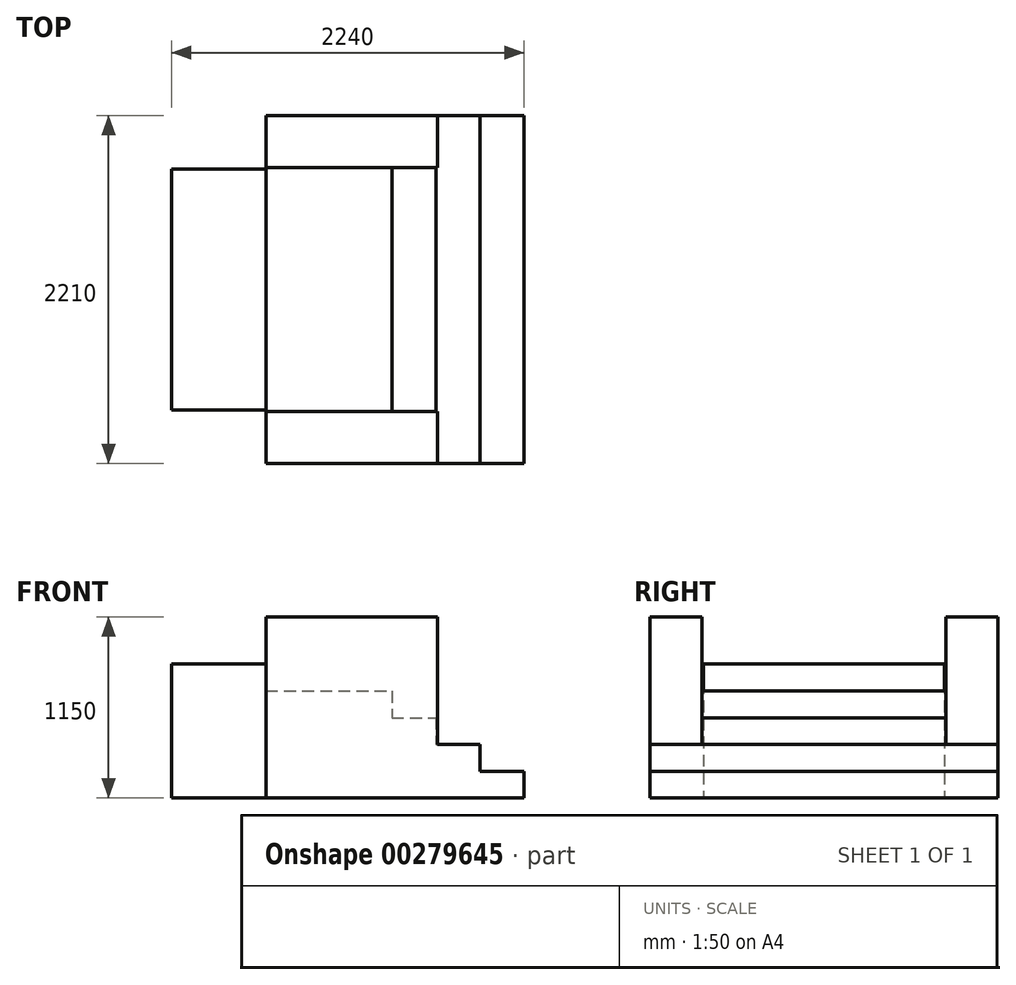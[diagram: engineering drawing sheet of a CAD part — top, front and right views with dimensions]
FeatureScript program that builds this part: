
annotation { "Feature Type Name" : "Feature", "Feature Type Description" : "" }
export const myFeature = defineFeature(function(context is Context, id is Id, definition is map)
    precondition{}
    {
        {
            var Q0;
            Q0=qCreatedBy(makeId("Front.planeOp"),FACE);
            var sketch = newSketch(context, id + "F0", { "sketchPlane" : qUnion([Q0])});
            skLineSegment(sketch, "E0", {"start": v(0, 0) * mm, "end": v(600, 0) * mm});
            skLineSegment(sketch, "E1", {"start": v(600, 0) * mm, "end": v(600, -170) * mm});
            skLineSegment(sketch, "E2", {"start": v(600, -170) * mm, "end": v(1400, -170) * mm});
            skLineSegment(sketch, "E3", {"start": v(1400, -170) * mm, "end": v(1400, -340) * mm});
            skLineSegment(sketch, "E4", {"start": v(1400, -340) * mm, "end": v(1680, -340) * mm});
            skLineSegment(sketch, "E5", {"start": v(1680, -340) * mm, "end": v(1680, -510) * mm});
            skLineSegment(sketch, "E6", {"start": v(1680, -510) * mm, "end": v(1960, -510) * mm});
            skLineSegment(sketch, "E7", {"start": v(1960, -510) * mm, "end": v(1960, -680) * mm});
            skLineSegment(sketch, "E8", {"start": v(1960, -680) * mm, "end": v(2240, -680) * mm});
            skLineSegment(sketch, "E9", {"start": v(2240, -680) * mm, "end": v(2240, -850) * mm});
            skLineSegment(sketch, "E10", {"start": v(0, 0) * mm, "end": v(0, -850) * mm});
            skLineSegment(sketch, "E11", {"start": v(0, -850) * mm, "end": v(2240, -850) * mm});
            skSolve(sketch);
        }
        {
            var Q0;
            Q0=makeQuery(id+"F0.imprint","IMPRINT",FACE,{"disambiguationData":[TD([[makeQuery(id+"F0.imprint","IMPRINT",EDGE,{"derivedFrom":sQuery(id+"F0.wireOp",EDGE,"E0")}),-1.0]])]});
            extrude(context, id + "F1", {"entities" : qUnion([Q0]), "endBound" : BoundingType.SYMMETRIC, "depth" : 2210 * mm});
        }
        {
            var Q0;
            Q0=makeQuery(id+"F1.opExtrude","CAP_FACE",FACE,{"disambiguationData":[OSD([sQuery(id+"F0.wireOp",EDGE,"E0"),sQuery(id+"F0.wireOp",EDGE,"E1"),sQuery(id+"F0.wireOp",EDGE,"E2"),sQuery(id+"F0.wireOp",EDGE,"E3"),sQuery(id+"F0.wireOp",EDGE,"E4"),sQuery(id+"F0.wireOp",EDGE,"E5"),sQuery(id+"F0.wireOp",EDGE,"E6"),sQuery(id+"F0.wireOp",EDGE,"E7"),sQuery(id+"F0.wireOp",EDGE,"E8"),sQuery(id+"F0.wireOp",EDGE,"E9"),sQuery(id+"F0.wireOp",EDGE,"E10"),sQuery(id+"F0.wireOp",EDGE,"E11")])],"isStart":false});
            var sketch = newSketch(context, id + "F2", { "sketchPlane" : qUnion([Q0])});
            skLineSegment(sketch, "E12.bottom", {"start": v(600, 0) * mm, "end": v(0, 0) * mm});
            skLineSegment(sketch, "E12.top", {"start": v(600, -850) * mm, "end": v(0, -850) * mm});
            skLineSegment(sketch, "E12.left", {"start": v(600, 0) * mm, "end": v(600, -850) * mm});
            skLineSegment(sketch, "E12.right", {"start": v(0, 0) * mm, "end": v(0, -850) * mm});
            skSolve(sketch);
        }
        {
            var Q0;
            {var subQ1=sQuery(id+"F2.wireOp",EDGE,"E12.bottom");Q0=makeQuery(id+"F2.imprint","IMPRINT",FACE,{"disambiguationData":[TD([[makeQuery(id+"F2.imprint","IMPRINT",EDGE,{"derivedFrom":subQ1}),-1.0]])]});}
            extrude(context, id + "F3", {"entities" : qUnion([Q0]), "operationType" : NewBodyOperationType.REMOVE, "oppositeDirection" : true, "depth" : 340 * mm});
        }
        {
            var Q0;
            Q0=makeQuery(id+"F1.opExtrude","CAP_FACE",FACE,{"disambiguationData":[OSD([sQuery(id+"F0.wireOp",EDGE,"E0"),sQuery(id+"F0.wireOp",EDGE,"E1"),sQuery(id+"F0.wireOp",EDGE,"E2"),sQuery(id+"F0.wireOp",EDGE,"E3"),sQuery(id+"F0.wireOp",EDGE,"E4"),sQuery(id+"F0.wireOp",EDGE,"E5"),sQuery(id+"F0.wireOp",EDGE,"E6"),sQuery(id+"F0.wireOp",EDGE,"E7"),sQuery(id+"F0.wireOp",EDGE,"E8"),sQuery(id+"F0.wireOp",EDGE,"E9"),sQuery(id+"F0.wireOp",EDGE,"E10"),sQuery(id+"F0.wireOp",EDGE,"E11")])],"isStart":true});
            var sketch = newSketch(context, id + "F4", { "sketchPlane" : qUnion([Q0])});
            skLineSegment(sketch, "E13.bottom", {"start": v(-600, 0) * mm, "end": v(0, 0) * mm});
            skLineSegment(sketch, "E13.top", {"start": v(-600, -850) * mm, "end": v(0, -850) * mm});
            skLineSegment(sketch, "E13.left", {"start": v(-600, 0) * mm, "end": v(-600, -850) * mm});
            skLineSegment(sketch, "E13.right", {"start": v(0, 0) * mm, "end": v(0, -850) * mm});
            skSolve(sketch);
        }
        {
            var Q0;
            {var subQ1=sQuery(id+"F4.wireOp",EDGE,"E13.bottom");Q0=makeQuery(id+"F4.imprint","IMPRINT",FACE,{"disambiguationData":[TD([[makeQuery(id+"F4.imprint","IMPRINT",EDGE,{"derivedFrom":subQ1}),1.0]])]});}
            extrude(context, id + "F5", {"entities" : qUnion([Q0]), "operationType" : NewBodyOperationType.REMOVE, "oppositeDirection" : true, "depth" : 340 * mm});
        }
        {
            var Q0;
            Q0=makeQuery(id+"F1.opExtrude","CAP_FACE",FACE,{"disambiguationData":[OSD([sQuery(id+"F0.wireOp",EDGE,"E0"),sQuery(id+"F0.wireOp",EDGE,"E1"),sQuery(id+"F0.wireOp",EDGE,"E2"),sQuery(id+"F0.wireOp",EDGE,"E3"),sQuery(id+"F0.wireOp",EDGE,"E4"),sQuery(id+"F0.wireOp",EDGE,"E5"),sQuery(id+"F0.wireOp",EDGE,"E6"),sQuery(id+"F0.wireOp",EDGE,"E7"),sQuery(id+"F0.wireOp",EDGE,"E8"),sQuery(id+"F0.wireOp",EDGE,"E9"),sQuery(id+"F0.wireOp",EDGE,"E10"),sQuery(id+"F0.wireOp",EDGE,"E11")])],"isStart":false});
            var sketch = newSketch(context, id + "F6", { "sketchPlane" : qUnion([Q0])});
            skLineSegment(sketch, "E14", {"start": v(600, -170) * mm, "end": v(600, 300) * mm});
            skLineSegment(sketch, "E15", {"start": v(600, 300) * mm, "end": v(1690, 300) * mm});
            skLineSegment(sketch, "E16", {"start": v(1690, 300) * mm, "end": v(1690, -510) * mm});
            skLineSegment(sketch, "E17.0", {"start": v(600, -170) * mm, "end": v(1400, -170) * mm});
            skLineSegment(sketch, "E18.0", {"start": v(1400, -170) * mm, "end": v(1400, -340) * mm});
            skLineSegment(sketch, "E19.0", {"start": v(1400, -340) * mm, "end": v(1680, -340) * mm});
            skLineSegment(sketch, "E20.0", {"start": v(1680, -340) * mm, "end": v(1680, -510) * mm});
            skLineSegment(sketch, "E21.0", {"start": v(1680, -510) * mm, "end": v(1690, -510) * mm});
            skPoint(sketch, "E22.orphan", {"position": v(1960, -510) * mm});
            skSolve(sketch);
        }
        {
            var Q0;
            Q0=makeQuery(id+"F6.imprint","IMPRINT",FACE,{"disambiguationData":[TD([[makeQuery(id+"F6.imprint","IMPRINT",EDGE,{"derivedFrom":sQuery(id+"F6.wireOp",EDGE,"E14")}),-1.0]])]});
            extrude(context, id + "F7", {"entities" : qUnion([Q0]), "operationType" : NewBodyOperationType.ADD, "oppositeDirection" : true, "depth" : 330 * mm});
        }
        {
            var Q0;
            Q0=makeQuery(id+"F1.opExtrude","CAP_FACE",FACE,{"disambiguationData":[OSD([sQuery(id+"F0.wireOp",EDGE,"E0"),sQuery(id+"F0.wireOp",EDGE,"E1"),sQuery(id+"F0.wireOp",EDGE,"E2"),sQuery(id+"F0.wireOp",EDGE,"E3"),sQuery(id+"F0.wireOp",EDGE,"E4"),sQuery(id+"F0.wireOp",EDGE,"E5"),sQuery(id+"F0.wireOp",EDGE,"E6"),sQuery(id+"F0.wireOp",EDGE,"E7"),sQuery(id+"F0.wireOp",EDGE,"E8"),sQuery(id+"F0.wireOp",EDGE,"E9"),sQuery(id+"F0.wireOp",EDGE,"E10"),sQuery(id+"F0.wireOp",EDGE,"E11")])],"isStart":true});
            var sketch = newSketch(context, id + "F8", { "sketchPlane" : qUnion([Q0])});
            skLineSegment(sketch, "E23.0", {"start": v(-1680, -510) * mm, "end": v(-1690, -510) * mm});
            skLineSegment(sketch, "E24.0", {"start": v(-1680, -340) * mm, "end": v(-1680, -510) * mm});
            skLineSegment(sketch, "E25.0", {"start": v(-1400, -340) * mm, "end": v(-1680, -340) * mm});
            skLineSegment(sketch, "E26.0", {"start": v(-1400, -170) * mm, "end": v(-1400, -340) * mm});
            skLineSegment(sketch, "E27.0", {"start": v(-600, -170) * mm, "end": v(-1400, -170) * mm});
            skLineSegment(sketch, "E28.0", {"start": v(-600, -170) * mm, "end": v(-600, 300) * mm});
            skLineSegment(sketch, "E29.0", {"start": v(-600, 300) * mm, "end": v(-1690, 300) * mm});
            skLineSegment(sketch, "E30.0", {"start": v(-1690, 300) * mm, "end": v(-1690, -510) * mm});
            skPoint(sketch, "E31.orphan", {"position": v(-1960, -510) * mm});
            skSolve(sketch);
        }
        {
            var Q0;
            Q0=makeQuery(id+"F8.imprint","IMPRINT",FACE,{"disambiguationData":[TD([[makeQuery(id+"F8.imprint","IMPRINT",EDGE,{"derivedFrom":sQuery(id+"F8.wireOp",EDGE,"E23.0")}),-1.0]])]});
            extrude(context, id + "F9", {"entities" : qUnion([Q0]), "operationType" : NewBodyOperationType.ADD, "oppositeDirection" : true, "depth" : 330 * mm});
        }
    });
